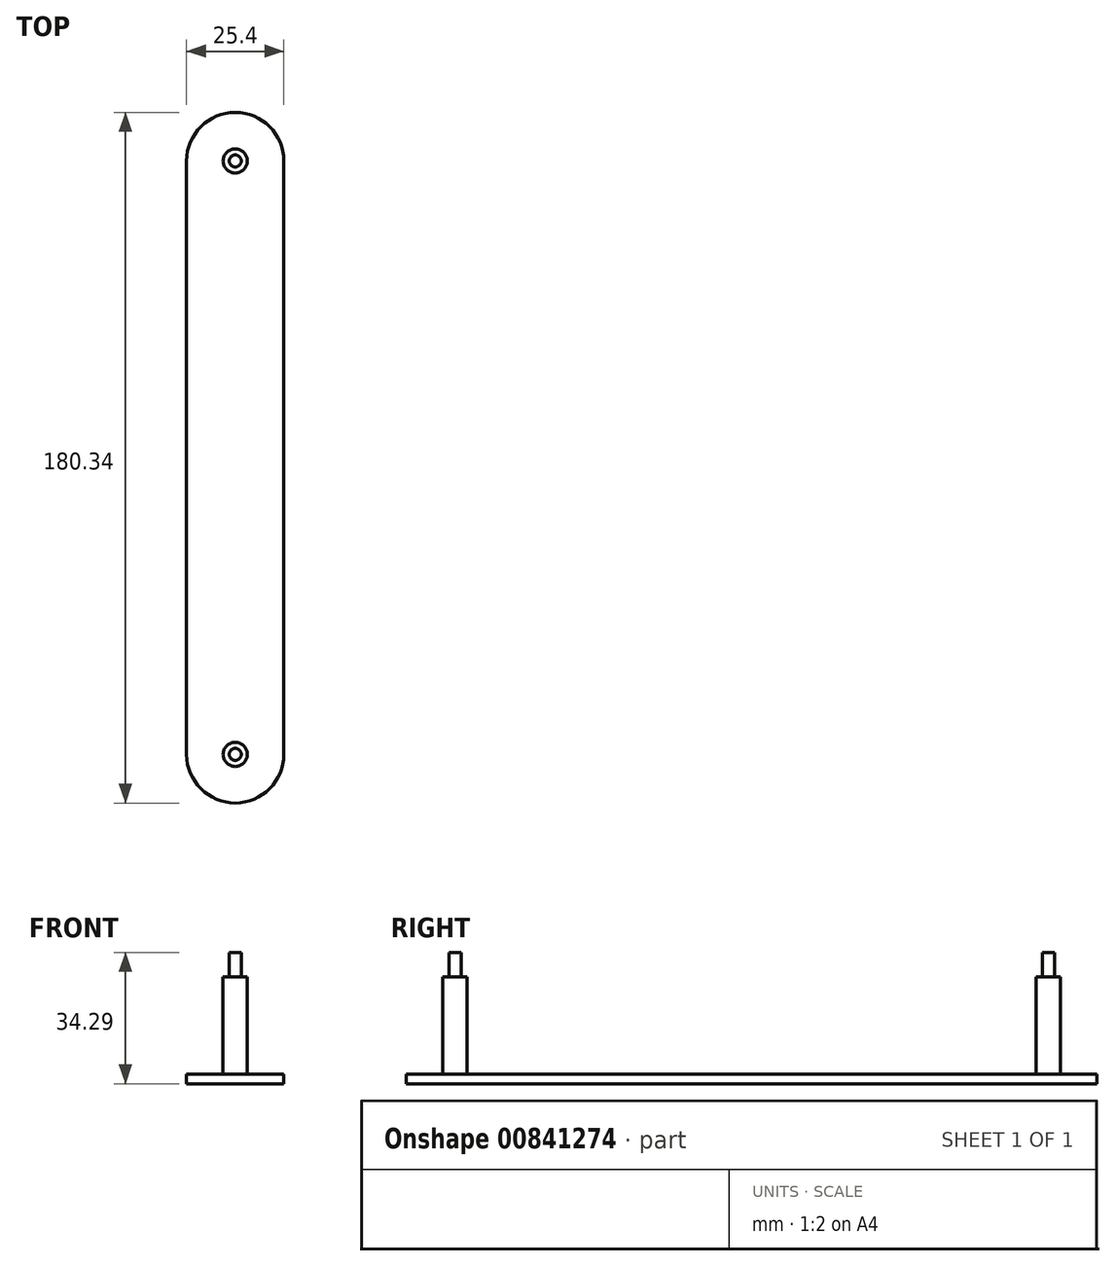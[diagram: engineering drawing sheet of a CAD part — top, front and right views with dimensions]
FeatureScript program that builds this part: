
annotation { "Feature Type Name" : "Feature", "Feature Type Description" : "" }
export const myFeature = defineFeature(function(context is Context, id is Id, definition is map)
    precondition{}
    {
        {
            var Q0;
            Q0=qCreatedBy(makeId("Top.planeOp"),FACE);
            var sketch = newSketch(context, id + "F0", { "sketchPlane" : qUnion([Q0])});
            skCircle(sketch, "E0", {"center": v(0, 154.94) * mm, "radius": 3.18 * mm});
            skCircle(sketch, "E1", {"center": v(0, 0) * mm, "radius": 3.18 * mm});
            skCircle(sketch, "E2", {"center": v(0, 154.94) * mm, "radius": 1.59 * mm});
            skCircle(sketch, "E3", {"center": v(0, 0) * mm, "radius": 1.59 * mm});
            skLineSegment(sketch, "E4", {"start": v(0, 154.94) * mm, "end": v(0, 0) * mm, "construction": true});
            skLineSegment(sketch, "E5", {"start": v(0, 167.64) * mm, "end": v(12.7, 167.64) * mm});
            skLineSegment(sketch, "E6", {"start": v(12.7, 167.64) * mm, "end": v(12.7, -12.7) * mm});
            skLineSegment(sketch, "E7", {"start": v(12.7, -12.7) * mm, "end": v(0, -12.7) * mm});
            skLineSegment(sketch, "E8.MirrorCS", {"start": v(-12.7, -12.7) * mm, "end": v(0, -12.7) * mm});
            skLineSegment(sketch, "E9.MirrorCS", {"start": v(0, 167.64) * mm, "end": v(-12.7, 167.64) * mm});
            skLineSegment(sketch, "E10.MirrorCS", {"start": v(-12.7, 167.64) * mm, "end": v(-12.7, -12.7) * mm});
            skSolve(sketch);
        }
        {
            var Q0;
            Q0=makeQuery(id+"F0.imprint","IMPRINT",FACE,{"disambiguationData":[TD([[makeQuery(id+"F0.imprint","IMPRINT",EDGE,{"derivedFrom":sQuery(id+"F0.wireOp",EDGE,"E0")}),-1.0]])]});
            var Q1;
            Q1=makeQuery(id+"F0.imprint","IMPRINT",FACE,{"disambiguationData":[TD([[makeQuery(id+"F0.imprint","IMPRINT",EDGE,{"derivedFrom":sQuery(id+"F0.wireOp",EDGE,"E0")}),1.0]])]});
            var Q2;
            Q2=makeQuery(id+"F0.imprint","IMPRINT",FACE,{"disambiguationData":[TD([[makeQuery(id+"F0.imprint","IMPRINT",EDGE,{"derivedFrom":sQuery(id+"F0.wireOp",EDGE,"E2")}),1.0]])]});
            var Q3;
            Q3=makeQuery(id+"F0.imprint","IMPRINT",FACE,{"disambiguationData":[TD([[makeQuery(id+"F0.imprint","IMPRINT",EDGE,{"derivedFrom":sQuery(id+"F0.wireOp",EDGE,"E1")}),1.0]])]});
            var Q4;
            Q4=makeQuery(id+"F0.imprint","IMPRINT",FACE,{"disambiguationData":[TD([[makeQuery(id+"F0.imprint","IMPRINT",EDGE,{"derivedFrom":sQuery(id+"F0.wireOp",EDGE,"E3")}),1.0]])]});
            extrude(context, id + "F1", {"entities" : qUnion([Q0, Q1, Q2, Q3, Q4]), "oppositeDirection" : true, "depth" : 2.54 * mm, "offsetDistance" : 25.4 * mm});
        }
        {
            var Q0;
            Q0=makeQuery(id+"F0.imprint","IMPRINT",FACE,{"disambiguationData":[TD([[makeQuery(id+"F0.imprint","IMPRINT",EDGE,{"derivedFrom":sQuery(id+"F0.wireOp",EDGE,"E0")}),1.0]])]});
            var Q1;
            Q1=makeQuery(id+"F0.imprint","IMPRINT",FACE,{"disambiguationData":[TD([[makeQuery(id+"F0.imprint","IMPRINT",EDGE,{"derivedFrom":sQuery(id+"F0.wireOp",EDGE,"E2")}),1.0]])]});
            var Q2;
            Q2=makeQuery(id+"F0.imprint","IMPRINT",FACE,{"disambiguationData":[TD([[makeQuery(id+"F0.imprint","IMPRINT",EDGE,{"derivedFrom":sQuery(id+"F0.wireOp",EDGE,"E3")}),1.0]])]});
            var Q3;
            Q3=makeQuery(id+"F0.imprint","IMPRINT",FACE,{"disambiguationData":[TD([[makeQuery(id+"F0.imprint","IMPRINT",EDGE,{"derivedFrom":sQuery(id+"F0.wireOp",EDGE,"E1")}),1.0]])]});
            extrude(context, id + "F2", {"entities" : qUnion([Q0, Q1, Q2, Q3]), "operationType" : NewBodyOperationType.ADD, "depth" : 25.4 * mm, "offsetDistance" : 25.4 * mm});
        }
        {
            var Q0;
            Q0=makeQuery(id+"F1.opExtrude","SWEPT_EDGE",EDGE,{"disambiguationData":[OSD([sQuery(id+"F0.wireOp",EDGE,"E5"),sQuery(id+"F0.wireOp",EDGE,"E6")])]});
            var Q1;
            Q1=makeQuery(id+"F1.opExtrude","SWEPT_EDGE",EDGE,{"disambiguationData":[OSD([sQuery(id+"F0.wireOp",EDGE,"E9.MirrorCS"),sQuery(id+"F0.wireOp",EDGE,"E10.MirrorCS")])]});
            var Q2;
            Q2=makeQuery(id+"F1.opExtrude","SWEPT_EDGE",EDGE,{"disambiguationData":[OSD([sQuery(id+"F0.wireOp",EDGE,"E8.MirrorCS"),sQuery(id+"F0.wireOp",EDGE,"E10.MirrorCS")])]});
            var Q3;
            Q3=makeQuery(id+"F1.opExtrude","SWEPT_EDGE",EDGE,{"disambiguationData":[OSD([sQuery(id+"F0.wireOp",EDGE,"E6"),sQuery(id+"F0.wireOp",EDGE,"E7")])]});
            fillet(context, id + "F3", {"entities" : qUnion([Q0, Q1, Q2, Q3]), "radius" : 12.7 * mm, "tangentPropagation" : true, "allowEdgeOverflow" : false});
        }
        {
            var Q0;
            Q0=makeQuery(id+"F0.imprint","IMPRINT",FACE,{"disambiguationData":[TD([[makeQuery(id+"F0.imprint","IMPRINT",EDGE,{"derivedFrom":sQuery(id+"F0.wireOp",EDGE,"E3")}),1.0]])]});
            var Q1;
            Q1=makeQuery(id+"F0.imprint","IMPRINT",FACE,{"disambiguationData":[TD([[makeQuery(id+"F0.imprint","IMPRINT",EDGE,{"derivedFrom":sQuery(id+"F0.wireOp",EDGE,"E2")}),1.0]])]});
            extrude(context, id + "F4", {"entities" : qUnion([Q0, Q1]), "operationType" : NewBodyOperationType.ADD, "depth" : 31.75 * mm, "offsetDistance" : 25.4 * mm});
        }
    });
